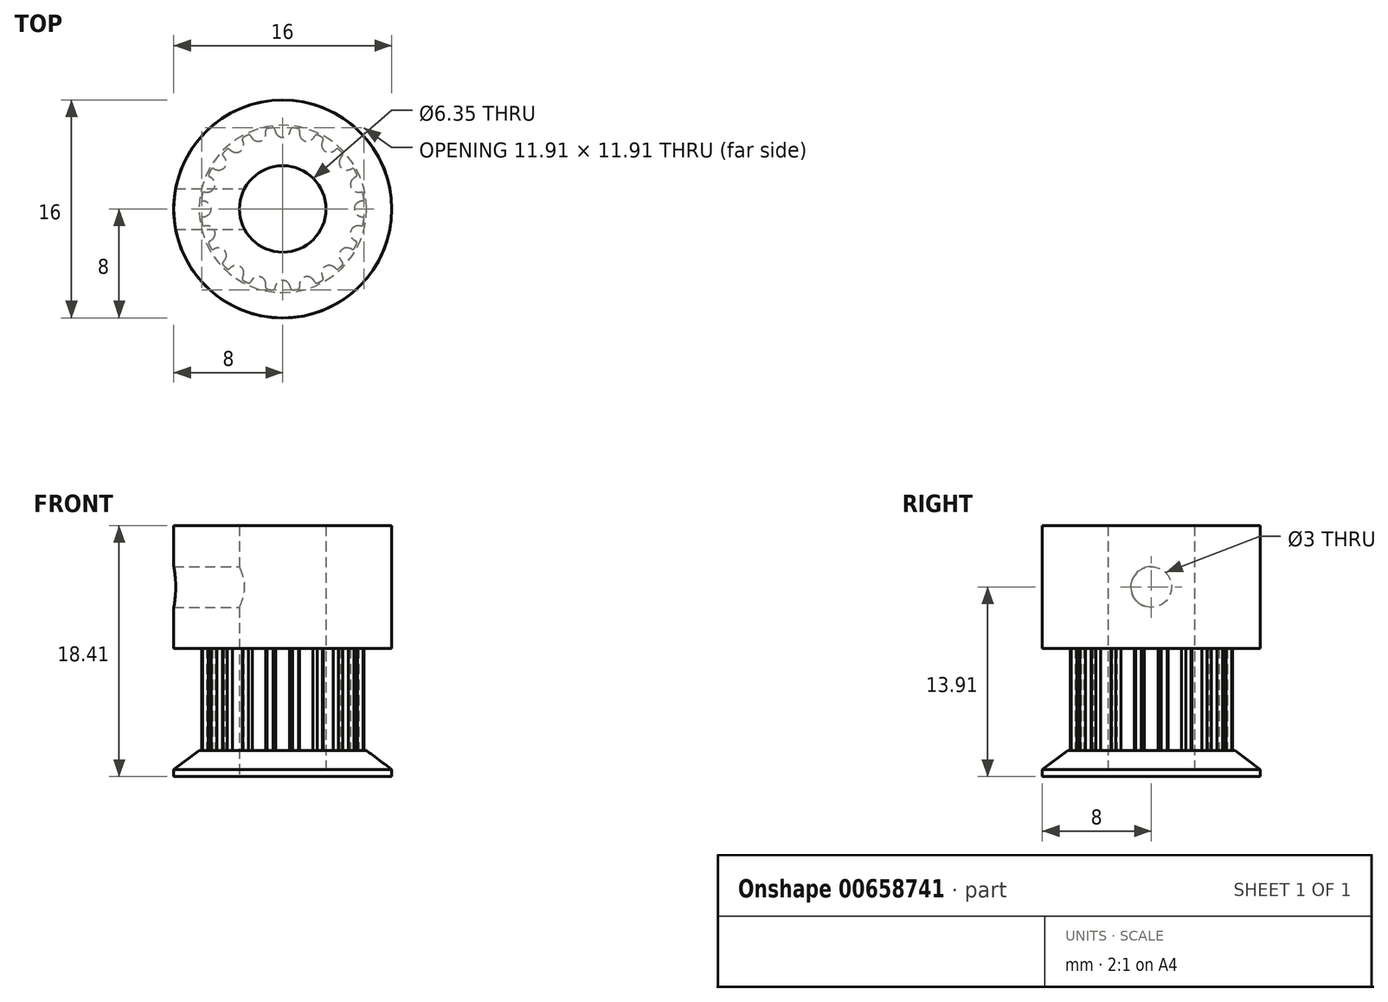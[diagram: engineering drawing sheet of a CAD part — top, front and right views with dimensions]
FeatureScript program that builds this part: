
annotation { "Feature Type Name" : "Feature", "Feature Type Description" : "" }
export const myFeature = defineFeature(function(context is Context, id is Id, definition is map)
    precondition{}
    {
        {
            var Q0;
            Q0=qCreatedBy(makeId("Top.planeOp"),FACE);
            var sketch = newSketch(context, id + "F0", { "sketchPlane" : qUnion([Q0])});
            skLineSegment(sketch, "E0", {"start": v(-19.17, 17.78) * mm, "end": v(-18.17, 17.78) * mm});
            skLineSegment(sketch, "E1", {"start": v(-18.17, 17.78) * mm, "end": v(-18.17, 18.4) * mm});
            skArc(sketch, "E2", {"start": v(-18.67, 18.85) * mm, "mid": v(-18.88, 19.07) * mm, "end": v(-19.17, 19.16) * mm});
            skArc(sketch, "E3", {"start": v(-18.58, 18.54) * mm, "mid": v(-18.61, 18.7) * mm, "end": v(-18.67, 18.85) * mm});
            skArc(sketch, "E4", {"start": v(-18.58, 18.54) * mm, "mid": v(-18.53, 18.44) * mm, "end": v(-18.43, 18.4) * mm});
            skLineSegment(sketch, "E5", {"start": v(-18.43, 18.4) * mm, "end": v(-18.17, 18.4) * mm});
            skArc(sketch, "E6.0.MirrorCS", {"start": v(-19.67, 18.85) * mm, "mid": v(-19.47, 19.07) * mm, "end": v(-19.17, 19.16) * mm});
            skArc(sketch, "E7.0.MirrorCS", {"start": v(-19.76, 18.54) * mm, "mid": v(-19.73, 18.7) * mm, "end": v(-19.67, 18.85) * mm});
            skArc(sketch, "E8.0.MirrorCS", {"start": v(-19.76, 18.54) * mm, "mid": v(-19.81, 18.44) * mm, "end": v(-19.91, 18.4) * mm});
            skLineSegment(sketch, "E9.0.MirrorCS", {"start": v(-19.91, 18.4) * mm, "end": v(-20.17, 18.4) * mm});
            skLineSegment(sketch, "E10.0.MirrorCS", {"start": v(-20.17, 17.78) * mm, "end": v(-20.17, 18.4) * mm});
            skLineSegment(sketch, "E11.0.MirrorCS", {"start": v(-19.17, 17.78) * mm, "end": v(-20.17, 17.78) * mm});
            skLineSegment(sketch, "E12.direction1", {"start": v(-20.17, 17.78) * mm, "end": v(-18.17, 17.78) * mm, "construction": true});
            skLineSegment(sketch, "E13", {"start": v(-20.17, 18.15) * mm, "end": v(-18.17, 18.15) * mm, "construction": true});
            skPoint(sketch, "E14", {"position": v(0, -5.25) * mm});
            skArc(sketch, "E15", {"start": v(0.51, -5.6) * mm, "mid": v(0, -5.25) * mm, "end": v(-0.51, -5.6) * mm});
            skArc(sketch, "E16", {"start": v(-0.51, -5.6) * mm, "mid": v(-0.56, -5.71) * mm, "end": v(-0.59, -5.83) * mm});
            skArc(sketch, "E17", {"start": v(0.59, -5.83) * mm, "mid": v(0.56, -5.71) * mm, "end": v(0.51, -5.6) * mm});
            skArc(sketch, "E18", {"start": v(0.72, -5.96) * mm, "mid": v(0.94, -5.93) * mm, "end": v(1.16, -5.89) * mm});
            skArc(sketch, "E19", {"start": v(0.59, -5.83) * mm, "mid": v(0.66, -5.94) * mm, "end": v(0.8, -5.95) * mm});
            skArc(sketch, "E20", {"start": v(-0.59, -5.83) * mm, "mid": v(-0.66, -5.94) * mm, "end": v(-0.8, -5.95) * mm});
            skArc(sketch, "E21.1.0", {"start": v(2.22, -5.16) * mm, "mid": v(1.62, -5) * mm, "end": v(1.24, -5.48) * mm});
            skPoint(sketch, "E21.1.1", {"position": v(1.62, -5) * mm});
            skArc(sketch, "E21.1.2", {"start": v(1.24, -5.48) * mm, "mid": v(1.23, -5.6) * mm, "end": v(1.24, -5.73) * mm});
            skArc(sketch, "E21.1.3", {"start": v(2.36, -5.37) * mm, "mid": v(2.47, -5.44) * mm, "end": v(2.6, -5.41) * mm});
            skArc(sketch, "E21.1.4", {"start": v(1.24, -5.73) * mm, "mid": v(1.2, -5.85) * mm, "end": v(1.08, -5.9) * mm});
            skArc(sketch, "E21.1.5", {"start": v(2.36, -5.37) * mm, "mid": v(2.3, -5.26) * mm, "end": v(2.22, -5.16) * mm});
            skArc(sketch, "E22.3.2.0", {"start": v(3.7, -4.22) * mm, "mid": v(3.09, -4.25) * mm, "end": v(2.87, -4.83) * mm});
            skPoint(sketch, "E22.4.2.0", {"position": v(3.09, -4.25) * mm});
            skArc(sketch, "E22.5.2.0", {"start": v(2.87, -4.83) * mm, "mid": v(2.9, -4.95) * mm, "end": v(2.95, -5.07) * mm});
            skArc(sketch, "E22.9.2.0", {"start": v(3.9, -4.37) * mm, "mid": v(4.03, -4.41) * mm, "end": v(4.14, -4.35) * mm});
            skArc(sketch, "E22.13.2.0", {"start": v(2.95, -5.07) * mm, "mid": v(2.95, -5.2) * mm, "end": v(2.85, -5.28) * mm});
            skArc(sketch, "E22.17.2.0", {"start": v(3.9, -4.37) * mm, "mid": v(3.81, -4.3) * mm, "end": v(3.7, -4.22) * mm});
            skArc(sketch, "E22.3.3.0", {"start": v(4.83, -2.87) * mm, "mid": v(4.25, -3.09) * mm, "end": v(4.22, -3.7) * mm});
            skPoint(sketch, "E22.4.3.0", {"position": v(4.25, -3.09) * mm});
            skArc(sketch, "E22.5.3.0", {"start": v(4.22, -3.7) * mm, "mid": v(4.3, -3.81) * mm, "end": v(4.37, -3.9) * mm});
            skArc(sketch, "E22.9.3.0", {"start": v(5.07, -2.95) * mm, "mid": v(5.2, -2.95) * mm, "end": v(5.28, -2.85) * mm});
            skArc(sketch, "E22.13.3.0", {"start": v(4.37, -3.9) * mm, "mid": v(4.41, -4.03) * mm, "end": v(4.35, -4.14) * mm});
            skArc(sketch, "E22.17.3.0", {"start": v(5.07, -2.95) * mm, "mid": v(4.95, -2.9) * mm, "end": v(4.83, -2.87) * mm});
            skArc(sketch, "E22.3.4.0", {"start": v(5.48, -1.24) * mm, "mid": v(5, -1.62) * mm, "end": v(5.16, -2.22) * mm});
            skPoint(sketch, "E22.4.4.0", {"position": v(5, -1.62) * mm});
            skArc(sketch, "E22.5.4.0", {"start": v(5.16, -2.22) * mm, "mid": v(5.26, -2.3) * mm, "end": v(5.37, -2.36) * mm});
            skArc(sketch, "E22.9.4.0", {"start": v(5.73, -1.24) * mm, "mid": v(5.85, -1.2) * mm, "end": v(5.9, -1.08) * mm});
            skArc(sketch, "E22.13.4.0", {"start": v(5.37, -2.36) * mm, "mid": v(5.44, -2.47) * mm, "end": v(5.41, -2.6) * mm});
            skArc(sketch, "E22.17.4.0", {"start": v(5.73, -1.24) * mm, "mid": v(5.6, -1.23) * mm, "end": v(5.48, -1.24) * mm});
            skArc(sketch, "E22.3.5.0", {"start": v(5.6, 0.51) * mm, "mid": v(5.25, 0) * mm, "end": v(5.6, -0.51) * mm});
            skPoint(sketch, "E22.4.5.0", {"position": v(5.25, 0) * mm});
            skArc(sketch, "E22.5.5.0", {"start": v(5.6, -0.51) * mm, "mid": v(5.71, -0.56) * mm, "end": v(5.83, -0.59) * mm});
            skArc(sketch, "E22.9.5.0", {"start": v(5.83, 0.59) * mm, "mid": v(5.94, 0.66) * mm, "end": v(5.95, 0.8) * mm});
            skArc(sketch, "E22.13.5.0", {"start": v(5.83, -0.59) * mm, "mid": v(5.94, -0.66) * mm, "end": v(5.95, -0.8) * mm});
            skArc(sketch, "E22.17.5.0", {"start": v(5.83, 0.59) * mm, "mid": v(5.71, 0.56) * mm, "end": v(5.6, 0.51) * mm});
            skArc(sketch, "E22.3.6.0", {"start": v(5.16, 2.22) * mm, "mid": v(5, 1.62) * mm, "end": v(5.48, 1.24) * mm});
            skPoint(sketch, "E22.4.6.0", {"position": v(5, 1.62) * mm});
            skArc(sketch, "E22.5.6.0", {"start": v(5.48, 1.24) * mm, "mid": v(5.6, 1.23) * mm, "end": v(5.73, 1.24) * mm});
            skArc(sketch, "E22.9.6.0", {"start": v(5.37, 2.36) * mm, "mid": v(5.44, 2.47) * mm, "end": v(5.41, 2.6) * mm});
            skArc(sketch, "E22.13.6.0", {"start": v(5.73, 1.24) * mm, "mid": v(5.85, 1.2) * mm, "end": v(5.9, 1.08) * mm});
            skArc(sketch, "E22.17.6.0", {"start": v(5.37, 2.36) * mm, "mid": v(5.26, 2.3) * mm, "end": v(5.16, 2.22) * mm});
            skArc(sketch, "E22.3.7.0", {"start": v(4.22, 3.7) * mm, "mid": v(4.25, 3.09) * mm, "end": v(4.83, 2.87) * mm});
            skPoint(sketch, "E22.4.7.0", {"position": v(4.25, 3.09) * mm});
            skArc(sketch, "E22.5.7.0", {"start": v(4.83, 2.87) * mm, "mid": v(4.95, 2.9) * mm, "end": v(5.07, 2.95) * mm});
            skArc(sketch, "E22.9.7.0", {"start": v(4.37, 3.9) * mm, "mid": v(4.41, 4.03) * mm, "end": v(4.35, 4.14) * mm});
            skArc(sketch, "E22.13.7.0", {"start": v(5.07, 2.95) * mm, "mid": v(5.2, 2.95) * mm, "end": v(5.28, 2.85) * mm});
            skArc(sketch, "E22.17.7.0", {"start": v(4.37, 3.9) * mm, "mid": v(4.3, 3.81) * mm, "end": v(4.22, 3.7) * mm});
            skArc(sketch, "E22.3.8.0", {"start": v(2.87, 4.83) * mm, "mid": v(3.09, 4.25) * mm, "end": v(3.7, 4.22) * mm});
            skPoint(sketch, "E22.4.8.0", {"position": v(3.09, 4.25) * mm});
            skArc(sketch, "E22.5.8.0", {"start": v(3.7, 4.22) * mm, "mid": v(3.81, 4.3) * mm, "end": v(3.9, 4.37) * mm});
            skArc(sketch, "E22.9.8.0", {"start": v(2.95, 5.07) * mm, "mid": v(2.95, 5.2) * mm, "end": v(2.85, 5.28) * mm});
            skArc(sketch, "E22.13.8.0", {"start": v(3.9, 4.37) * mm, "mid": v(4.03, 4.41) * mm, "end": v(4.14, 4.35) * mm});
            skArc(sketch, "E22.17.8.0", {"start": v(2.95, 5.07) * mm, "mid": v(2.9, 4.95) * mm, "end": v(2.87, 4.83) * mm});
            skArc(sketch, "E22.3.9.0", {"start": v(1.24, 5.48) * mm, "mid": v(1.62, 5) * mm, "end": v(2.22, 5.16) * mm});
            skPoint(sketch, "E22.4.9.0", {"position": v(1.62, 5) * mm});
            skArc(sketch, "E22.5.9.0", {"start": v(2.22, 5.16) * mm, "mid": v(2.3, 5.26) * mm, "end": v(2.36, 5.37) * mm});
            skArc(sketch, "E22.9.9.0", {"start": v(1.24, 5.73) * mm, "mid": v(1.2, 5.85) * mm, "end": v(1.08, 5.9) * mm});
            skArc(sketch, "E22.13.9.0", {"start": v(2.36, 5.37) * mm, "mid": v(2.47, 5.44) * mm, "end": v(2.6, 5.41) * mm});
            skArc(sketch, "E22.17.9.0", {"start": v(1.24, 5.73) * mm, "mid": v(1.23, 5.6) * mm, "end": v(1.24, 5.48) * mm});
            skArc(sketch, "E22.3.10.0", {"start": v(-0.51, 5.6) * mm, "mid": v(0, 5.25) * mm, "end": v(0.51, 5.6) * mm});
            skPoint(sketch, "E22.4.10.0", {"position": v(0, 5.25) * mm});
            skArc(sketch, "E22.5.10.0", {"start": v(0.51, 5.6) * mm, "mid": v(0.56, 5.71) * mm, "end": v(0.59, 5.83) * mm});
            skArc(sketch, "E22.9.10.0", {"start": v(-0.59, 5.83) * mm, "mid": v(-0.66, 5.94) * mm, "end": v(-0.8, 5.95) * mm});
            skArc(sketch, "E22.13.10.0", {"start": v(0.59, 5.83) * mm, "mid": v(0.66, 5.94) * mm, "end": v(0.8, 5.95) * mm});
            skArc(sketch, "E22.17.10.0", {"start": v(-0.59, 5.83) * mm, "mid": v(-0.56, 5.71) * mm, "end": v(-0.51, 5.6) * mm});
            skArc(sketch, "E22.3.11.0", {"start": v(-2.22, 5.16) * mm, "mid": v(-1.62, 5) * mm, "end": v(-1.24, 5.48) * mm});
            skPoint(sketch, "E22.4.11.0", {"position": v(-1.62, 5) * mm});
            skArc(sketch, "E22.5.11.0", {"start": v(-1.24, 5.48) * mm, "mid": v(-1.23, 5.6) * mm, "end": v(-1.24, 5.73) * mm});
            skArc(sketch, "E22.9.11.0", {"start": v(-2.36, 5.37) * mm, "mid": v(-2.47, 5.44) * mm, "end": v(-2.6, 5.41) * mm});
            skArc(sketch, "E22.13.11.0", {"start": v(-1.24, 5.73) * mm, "mid": v(-1.2, 5.85) * mm, "end": v(-1.08, 5.9) * mm});
            skArc(sketch, "E22.17.11.0", {"start": v(-2.36, 5.37) * mm, "mid": v(-2.3, 5.26) * mm, "end": v(-2.22, 5.16) * mm});
            skArc(sketch, "E22.3.12.0", {"start": v(-3.7, 4.22) * mm, "mid": v(-3.09, 4.25) * mm, "end": v(-2.87, 4.83) * mm});
            skPoint(sketch, "E22.4.12.0", {"position": v(-3.09, 4.25) * mm});
            skArc(sketch, "E22.5.12.0", {"start": v(-2.87, 4.83) * mm, "mid": v(-2.9, 4.95) * mm, "end": v(-2.95, 5.07) * mm});
            skArc(sketch, "E22.9.12.0", {"start": v(-3.9, 4.37) * mm, "mid": v(-4.03, 4.41) * mm, "end": v(-4.14, 4.35) * mm});
            skArc(sketch, "E22.13.12.0", {"start": v(-2.95, 5.07) * mm, "mid": v(-2.95, 5.2) * mm, "end": v(-2.85, 5.28) * mm});
            skArc(sketch, "E22.17.12.0", {"start": v(-3.9, 4.37) * mm, "mid": v(-3.81, 4.3) * mm, "end": v(-3.7, 4.22) * mm});
            skArc(sketch, "E22.3.13.0", {"start": v(-4.83, 2.87) * mm, "mid": v(-4.25, 3.09) * mm, "end": v(-4.22, 3.7) * mm});
            skPoint(sketch, "E22.4.13.0", {"position": v(-4.25, 3.09) * mm});
            skArc(sketch, "E22.5.13.0", {"start": v(-4.22, 3.7) * mm, "mid": v(-4.3, 3.81) * mm, "end": v(-4.37, 3.9) * mm});
            skArc(sketch, "E22.9.13.0", {"start": v(-5.07, 2.95) * mm, "mid": v(-5.2, 2.95) * mm, "end": v(-5.28, 2.85) * mm});
            skArc(sketch, "E22.13.13.0", {"start": v(-4.37, 3.9) * mm, "mid": v(-4.41, 4.03) * mm, "end": v(-4.35, 4.14) * mm});
            skArc(sketch, "E22.17.13.0", {"start": v(-5.07, 2.95) * mm, "mid": v(-4.95, 2.9) * mm, "end": v(-4.83, 2.87) * mm});
            skArc(sketch, "E22.3.14.0", {"start": v(-5.48, 1.24) * mm, "mid": v(-5, 1.62) * mm, "end": v(-5.16, 2.22) * mm});
            skPoint(sketch, "E22.4.14.0", {"position": v(-5, 1.62) * mm});
            skArc(sketch, "E22.5.14.0", {"start": v(-5.16, 2.22) * mm, "mid": v(-5.26, 2.3) * mm, "end": v(-5.37, 2.36) * mm});
            skArc(sketch, "E22.9.14.0", {"start": v(-5.73, 1.24) * mm, "mid": v(-5.85, 1.2) * mm, "end": v(-5.9, 1.08) * mm});
            skArc(sketch, "E22.13.14.0", {"start": v(-5.37, 2.36) * mm, "mid": v(-5.44, 2.47) * mm, "end": v(-5.41, 2.6) * mm});
            skArc(sketch, "E22.17.14.0", {"start": v(-5.73, 1.24) * mm, "mid": v(-5.6, 1.23) * mm, "end": v(-5.48, 1.24) * mm});
            skArc(sketch, "E22.3.15.0", {"start": v(-5.6, -0.51) * mm, "mid": v(-5.25, 0) * mm, "end": v(-5.6, 0.51) * mm});
            skPoint(sketch, "E22.4.15.0", {"position": v(-5.25, 0) * mm});
            skArc(sketch, "E22.5.15.0", {"start": v(-5.6, 0.51) * mm, "mid": v(-5.71, 0.56) * mm, "end": v(-5.83, 0.59) * mm});
            skArc(sketch, "E22.9.15.0", {"start": v(-5.83, -0.59) * mm, "mid": v(-5.94, -0.66) * mm, "end": v(-5.95, -0.8) * mm});
            skArc(sketch, "E22.13.15.0", {"start": v(-5.83, 0.59) * mm, "mid": v(-5.94, 0.66) * mm, "end": v(-5.95, 0.8) * mm});
            skArc(sketch, "E22.17.15.0", {"start": v(-5.83, -0.59) * mm, "mid": v(-5.71, -0.56) * mm, "end": v(-5.6, -0.51) * mm});
            skArc(sketch, "E22.3.16.0", {"start": v(-5.16, -2.22) * mm, "mid": v(-5, -1.62) * mm, "end": v(-5.48, -1.24) * mm});
            skPoint(sketch, "E22.4.16.0", {"position": v(-5, -1.62) * mm});
            skArc(sketch, "E22.5.16.0", {"start": v(-5.48, -1.24) * mm, "mid": v(-5.6, -1.23) * mm, "end": v(-5.73, -1.24) * mm});
            skArc(sketch, "E22.9.16.0", {"start": v(-5.37, -2.36) * mm, "mid": v(-5.44, -2.47) * mm, "end": v(-5.41, -2.6) * mm});
            skArc(sketch, "E22.13.16.0", {"start": v(-5.73, -1.24) * mm, "mid": v(-5.85, -1.2) * mm, "end": v(-5.9, -1.08) * mm});
            skArc(sketch, "E22.17.16.0", {"start": v(-5.37, -2.36) * mm, "mid": v(-5.26, -2.3) * mm, "end": v(-5.16, -2.22) * mm});
            skArc(sketch, "E22.3.17.0", {"start": v(-4.22, -3.7) * mm, "mid": v(-4.25, -3.09) * mm, "end": v(-4.83, -2.87) * mm});
            skPoint(sketch, "E22.4.17.0", {"position": v(-4.25, -3.09) * mm});
            skArc(sketch, "E22.5.17.0", {"start": v(-4.83, -2.87) * mm, "mid": v(-4.95, -2.9) * mm, "end": v(-5.07, -2.95) * mm});
            skArc(sketch, "E22.9.17.0", {"start": v(-4.37, -3.9) * mm, "mid": v(-4.41, -4.03) * mm, "end": v(-4.35, -4.14) * mm});
            skArc(sketch, "E22.13.17.0", {"start": v(-5.07, -2.95) * mm, "mid": v(-5.2, -2.95) * mm, "end": v(-5.28, -2.85) * mm});
            skArc(sketch, "E22.17.17.0", {"start": v(-4.37, -3.9) * mm, "mid": v(-4.3, -3.81) * mm, "end": v(-4.22, -3.7) * mm});
            skArc(sketch, "E22.3.18.0", {"start": v(-2.87, -4.83) * mm, "mid": v(-3.09, -4.25) * mm, "end": v(-3.7, -4.22) * mm});
            skPoint(sketch, "E22.4.18.0", {"position": v(-3.09, -4.25) * mm});
            skArc(sketch, "E22.5.18.0", {"start": v(-3.7, -4.22) * mm, "mid": v(-3.81, -4.3) * mm, "end": v(-3.9, -4.37) * mm});
            skArc(sketch, "E22.9.18.0", {"start": v(-2.95, -5.07) * mm, "mid": v(-2.95, -5.2) * mm, "end": v(-2.85, -5.28) * mm});
            skArc(sketch, "E22.13.18.0", {"start": v(-3.9, -4.37) * mm, "mid": v(-4.03, -4.41) * mm, "end": v(-4.14, -4.35) * mm});
            skArc(sketch, "E22.17.18.0", {"start": v(-2.95, -5.07) * mm, "mid": v(-2.9, -4.95) * mm, "end": v(-2.87, -4.83) * mm});
            skArc(sketch, "E22.3.19.0", {"start": v(-1.24, -5.48) * mm, "mid": v(-1.62, -5) * mm, "end": v(-2.22, -5.16) * mm});
            skPoint(sketch, "E22.4.19.0", {"position": v(-1.62, -5) * mm});
            skArc(sketch, "E22.5.19.0", {"start": v(-2.22, -5.16) * mm, "mid": v(-2.3, -5.26) * mm, "end": v(-2.36, -5.37) * mm});
            skArc(sketch, "E22.9.19.0", {"start": v(-1.24, -5.73) * mm, "mid": v(-1.2, -5.85) * mm, "end": v(-1.08, -5.9) * mm});
            skArc(sketch, "E22.13.19.0", {"start": v(-2.36, -5.37) * mm, "mid": v(-2.47, -5.44) * mm, "end": v(-2.6, -5.41) * mm});
            skArc(sketch, "E22.17.19.0", {"start": v(-1.24, -5.73) * mm, "mid": v(-1.23, -5.6) * mm, "end": v(-1.24, -5.48) * mm});
            skArc(sketch, "E23.trimOffspring", {"start": v(2.52, -5.44) * mm, "mid": v(2.72, -5.35) * mm, "end": v(2.92, -5.24) * mm});
            skArc(sketch, "E24.trimOffspring", {"start": v(4.08, -4.4) * mm, "mid": v(4.24, -4.24) * mm, "end": v(4.4, -4.08) * mm});
            skArc(sketch, "E25.trimOffspring", {"start": v(5.24, -2.92) * mm, "mid": v(5.33, -2.76) * mm, "end": v(5.41, -2.6) * mm});
            skArc(sketch, "E26.trimOffspring", {"start": v(5.89, -1.16) * mm, "mid": v(5.93, -0.94) * mm, "end": v(5.96, -0.72) * mm});
            skArc(sketch, "E27.trimOffspring", {"start": v(5.44, 2.52) * mm, "mid": v(5.35, 2.72) * mm, "end": v(5.24, 2.92) * mm});
            skArc(sketch, "E28.trimOffspring", {"start": v(4.4, 4.08) * mm, "mid": v(4.24, 4.24) * mm, "end": v(4.08, 4.4) * mm});
            skArc(sketch, "E29.trimOffspring", {"start": v(5.96, 0.72) * mm, "mid": v(5.93, 0.94) * mm, "end": v(5.89, 1.16) * mm});
            skArc(sketch, "E30.trimOffspring", {"start": v(2.92, 5.24) * mm, "mid": v(2.72, 5.35) * mm, "end": v(2.52, 5.44) * mm});
            skArc(sketch, "E31.trimOffspring", {"start": v(1.16, 5.89) * mm, "mid": v(0.94, 5.93) * mm, "end": v(0.72, 5.96) * mm});
            skArc(sketch, "E32.trimOffspring", {"start": v(-0.72, 5.96) * mm, "mid": v(-0.94, 5.93) * mm, "end": v(-1.16, 5.89) * mm});
            skArc(sketch, "E33.trimOffspring", {"start": v(-2.52, 5.44) * mm, "mid": v(-2.72, 5.35) * mm, "end": v(-2.92, 5.24) * mm});
            skArc(sketch, "E34.trimOffspring", {"start": v(-4.08, 4.4) * mm, "mid": v(-4.24, 4.24) * mm, "end": v(-4.4, 4.08) * mm});
            skArc(sketch, "E35.trimOffspring", {"start": v(-5.24, 2.92) * mm, "mid": v(-5.35, 2.72) * mm, "end": v(-5.44, 2.52) * mm});
            skArc(sketch, "E36.trimOffspring", {"start": v(-5.89, 1.16) * mm, "mid": v(-5.93, 0.94) * mm, "end": v(-5.96, 0.72) * mm});
            skArc(sketch, "E37.trimOffspring", {"start": v(-5.96, -0.72) * mm, "mid": v(-5.93, -0.94) * mm, "end": v(-5.89, -1.16) * mm});
            skArc(sketch, "E38.trimOffspring", {"start": v(-5.44, -2.52) * mm, "mid": v(-5.35, -2.72) * mm, "end": v(-5.24, -2.92) * mm});
            skArc(sketch, "E39.trimOffspring", {"start": v(-4.4, -4.08) * mm, "mid": v(-4.24, -4.24) * mm, "end": v(-4.08, -4.4) * mm});
            skArc(sketch, "E40.trimOffspring", {"start": v(-2.92, -5.24) * mm, "mid": v(-2.72, -5.35) * mm, "end": v(-2.52, -5.44) * mm});
            skArc(sketch, "E41.trimOffspring", {"start": v(-1.16, -5.89) * mm, "mid": v(-0.94, -5.93) * mm, "end": v(-0.72, -5.96) * mm});
            skSolve(sketch);
        }
        {
            var Q0;
            Q0=makeQuery(id+"F0.imprint","IMPRINT",FACE,{"disambiguationData":[TD([[makeQuery(id+"F0.imprint","IMPRINT",EDGE,{"derivedFrom":sQuery(id+"F0.wireOp",EDGE,"E15")}),-1.0]])]});
            extrude(context, id + "F1", {"entities" : qUnion([Q0]), "depth" : 7.5 * mm});
        }
        {
            var Q0;
            Q0=makeQuery(id+"F1.opExtrude","CAP_FACE",FACE,{"disambiguationData":[OSD([sQuery(id+"F0.wireOp",EDGE,"E15"),sQuery(id+"F0.wireOp",EDGE,"E16"),sQuery(id+"F0.wireOp",EDGE,"E17"),sQuery(id+"F0.wireOp",EDGE,"E18"),sQuery(id+"F0.wireOp",EDGE,"E19"),sQuery(id+"F0.wireOp",EDGE,"E20"),sQuery(id+"F0.wireOp",EDGE,"E21.1.0"),sQuery(id+"F0.wireOp",EDGE,"E21.1.2"),sQuery(id+"F0.wireOp",EDGE,"E21.1.3"),sQuery(id+"F0.wireOp",EDGE,"E21.1.4"),sQuery(id+"F0.wireOp",EDGE,"E21.1.5"),sQuery(id+"F0.wireOp",EDGE,"E22.3.2.0"),sQuery(id+"F0.wireOp",EDGE,"E22.5.2.0"),sQuery(id+"F0.wireOp",EDGE,"E22.9.2.0"),sQuery(id+"F0.wireOp",EDGE,"E22.13.2.0"),sQuery(id+"F0.wireOp",EDGE,"E22.17.2.0"),sQuery(id+"F0.wireOp",EDGE,"E22.3.3.0"),sQuery(id+"F0.wireOp",EDGE,"E22.5.3.0"),sQuery(id+"F0.wireOp",EDGE,"E22.9.3.0"),sQuery(id+"F0.wireOp",EDGE,"E22.13.3.0"),sQuery(id+"F0.wireOp",EDGE,"E22.17.3.0"),sQuery(id+"F0.wireOp",EDGE,"E22.3.4.0"),sQuery(id+"F0.wireOp",EDGE,"E22.5.4.0"),sQuery(id+"F0.wireOp",EDGE,"E22.9.4.0"),sQuery(id+"F0.wireOp",EDGE,"E22.13.4.0"),sQuery(id+"F0.wireOp",EDGE,"E22.17.4.0"),sQuery(id+"F0.wireOp",EDGE,"E22.3.5.0"),sQuery(id+"F0.wireOp",EDGE,"E22.5.5.0"),sQuery(id+"F0.wireOp",EDGE,"E22.9.5.0"),sQuery(id+"F0.wireOp",EDGE,"E22.13.5.0"),sQuery(id+"F0.wireOp",EDGE,"E22.17.5.0"),sQuery(id+"F0.wireOp",EDGE,"E22.3.6.0"),sQuery(id+"F0.wireOp",EDGE,"E22.5.6.0"),sQuery(id+"F0.wireOp",EDGE,"E22.9.6.0"),sQuery(id+"F0.wireOp",EDGE,"E22.13.6.0"),sQuery(id+"F0.wireOp",EDGE,"E22.17.6.0"),sQuery(id+"F0.wireOp",EDGE,"E22.3.7.0"),sQuery(id+"F0.wireOp",EDGE,"E22.5.7.0"),sQuery(id+"F0.wireOp",EDGE,"E22.9.7.0"),sQuery(id+"F0.wireOp",EDGE,"E22.13.7.0"),sQuery(id+"F0.wireOp",EDGE,"E22.17.7.0"),sQuery(id+"F0.wireOp",EDGE,"E22.3.8.0"),sQuery(id+"F0.wireOp",EDGE,"E22.5.8.0"),sQuery(id+"F0.wireOp",EDGE,"E22.9.8.0"),sQuery(id+"F0.wireOp",EDGE,"E22.13.8.0"),sQuery(id+"F0.wireOp",EDGE,"E22.17.8.0"),sQuery(id+"F0.wireOp",EDGE,"E22.3.9.0"),sQuery(id+"F0.wireOp",EDGE,"E22.5.9.0"),sQuery(id+"F0.wireOp",EDGE,"E22.9.9.0"),sQuery(id+"F0.wireOp",EDGE,"E22.13.9.0"),sQuery(id+"F0.wireOp",EDGE,"E22.17.9.0"),sQuery(id+"F0.wireOp",EDGE,"E22.3.10.0"),sQuery(id+"F0.wireOp",EDGE,"E22.5.10.0"),sQuery(id+"F0.wireOp",EDGE,"E22.9.10.0"),sQuery(id+"F0.wireOp",EDGE,"E22.13.10.0"),sQuery(id+"F0.wireOp",EDGE,"E22.17.10.0"),sQuery(id+"F0.wireOp",EDGE,"E22.3.11.0"),sQuery(id+"F0.wireOp",EDGE,"E22.5.11.0"),sQuery(id+"F0.wireOp",EDGE,"E22.9.11.0"),sQuery(id+"F0.wireOp",EDGE,"E22.13.11.0"),sQuery(id+"F0.wireOp",EDGE,"E22.17.11.0"),sQuery(id+"F0.wireOp",EDGE,"E22.3.12.0"),sQuery(id+"F0.wireOp",EDGE,"E22.5.12.0"),sQuery(id+"F0.wireOp",EDGE,"E22.9.12.0"),sQuery(id+"F0.wireOp",EDGE,"E22.13.12.0"),sQuery(id+"F0.wireOp",EDGE,"E22.17.12.0"),sQuery(id+"F0.wireOp",EDGE,"E22.3.13.0"),sQuery(id+"F0.wireOp",EDGE,"E22.5.13.0"),sQuery(id+"F0.wireOp",EDGE,"E22.9.13.0"),sQuery(id+"F0.wireOp",EDGE,"E22.13.13.0"),sQuery(id+"F0.wireOp",EDGE,"E22.17.13.0"),sQuery(id+"F0.wireOp",EDGE,"E22.3.14.0"),sQuery(id+"F0.wireOp",EDGE,"E22.5.14.0"),sQuery(id+"F0.wireOp",EDGE,"E22.9.14.0"),sQuery(id+"F0.wireOp",EDGE,"E22.13.14.0"),sQuery(id+"F0.wireOp",EDGE,"E22.17.14.0"),sQuery(id+"F0.wireOp",EDGE,"E22.3.15.0"),sQuery(id+"F0.wireOp",EDGE,"E22.5.15.0"),sQuery(id+"F0.wireOp",EDGE,"E22.9.15.0"),sQuery(id+"F0.wireOp",EDGE,"E22.13.15.0"),sQuery(id+"F0.wireOp",EDGE,"E22.17.15.0"),sQuery(id+"F0.wireOp",EDGE,"E22.3.16.0"),sQuery(id+"F0.wireOp",EDGE,"E22.5.16.0"),sQuery(id+"F0.wireOp",EDGE,"E22.9.16.0"),sQuery(id+"F0.wireOp",EDGE,"E22.13.16.0"),sQuery(id+"F0.wireOp",EDGE,"E22.17.16.0"),sQuery(id+"F0.wireOp",EDGE,"E22.3.17.0"),sQuery(id+"F0.wireOp",EDGE,"E22.5.17.0"),sQuery(id+"F0.wireOp",EDGE,"E22.9.17.0"),sQuery(id+"F0.wireOp",EDGE,"E22.13.17.0"),sQuery(id+"F0.wireOp",EDGE,"E22.17.17.0"),sQuery(id+"F0.wireOp",EDGE,"E22.3.18.0"),sQuery(id+"F0.wireOp",EDGE,"E22.5.18.0"),sQuery(id+"F0.wireOp",EDGE,"E22.9.18.0"),sQuery(id+"F0.wireOp",EDGE,"E22.13.18.0"),sQuery(id+"F0.wireOp",EDGE,"E22.17.18.0"),sQuery(id+"F0.wireOp",EDGE,"E22.3.19.0"),sQuery(id+"F0.wireOp",EDGE,"E22.5.19.0"),sQuery(id+"F0.wireOp",EDGE,"E22.9.19.0"),sQuery(id+"F0.wireOp",EDGE,"E22.13.19.0"),sQuery(id+"F0.wireOp",EDGE,"E22.17.19.0"),sQuery(id+"F0.wireOp",EDGE,"E23.trimOffspring"),sQuery(id+"F0.wireOp",EDGE,"E24.trimOffspring"),sQuery(id+"F0.wireOp",EDGE,"E25.trimOffspring"),sQuery(id+"F0.wireOp",EDGE,"E26.trimOffspring"),sQuery(id+"F0.wireOp",EDGE,"E27.trimOffspring"),sQuery(id+"F0.wireOp",EDGE,"E28.trimOffspring"),sQuery(id+"F0.wireOp",EDGE,"E29.trimOffspring"),sQuery(id+"F0.wireOp",EDGE,"E30.trimOffspring"),sQuery(id+"F0.wireOp",EDGE,"E31.trimOffspring"),sQuery(id+"F0.wireOp",EDGE,"E32.trimOffspring"),sQuery(id+"F0.wireOp",EDGE,"E33.trimOffspring"),sQuery(id+"F0.wireOp",EDGE,"E34.trimOffspring"),sQuery(id+"F0.wireOp",EDGE,"E35.trimOffspring"),sQuery(id+"F0.wireOp",EDGE,"E36.trimOffspring"),sQuery(id+"F0.wireOp",EDGE,"E37.trimOffspring"),sQuery(id+"F0.wireOp",EDGE,"E38.trimOffspring"),sQuery(id+"F0.wireOp",EDGE,"E39.trimOffspring"),sQuery(id+"F0.wireOp",EDGE,"E40.trimOffspring"),sQuery(id+"F0.wireOp",EDGE,"E41.trimOffspring")])],"isStart":false});
            var sketch = newSketch(context, id + "F2", { "sketchPlane" : qUnion([Q0])});
            skCircle(sketch, "E42", {"center": v(0, 0) * mm, "radius": 8 * mm});
            skSolve(sketch);
        }
        {
            var Q0;
            Q0=qSketchRegion(id+"F2",true);
            extrude(context, id + "F3", {"entities" : qUnion([Q0]), "operationType" : NewBodyOperationType.ADD, "depth" : 9 * mm});
        }
        {
            var Q0;
            Q0=makeQuery(id+"F1.opExtrude","CAP_FACE",FACE,{"disambiguationData":[OSD([sQuery(id+"F0.wireOp",EDGE,"E15"),sQuery(id+"F0.wireOp",EDGE,"E16"),sQuery(id+"F0.wireOp",EDGE,"E17"),sQuery(id+"F0.wireOp",EDGE,"E18"),sQuery(id+"F0.wireOp",EDGE,"E19"),sQuery(id+"F0.wireOp",EDGE,"E20"),sQuery(id+"F0.wireOp",EDGE,"E21.1.0"),sQuery(id+"F0.wireOp",EDGE,"E21.1.2"),sQuery(id+"F0.wireOp",EDGE,"E21.1.3"),sQuery(id+"F0.wireOp",EDGE,"E21.1.4"),sQuery(id+"F0.wireOp",EDGE,"E21.1.5"),sQuery(id+"F0.wireOp",EDGE,"E22.3.2.0"),sQuery(id+"F0.wireOp",EDGE,"E22.5.2.0"),sQuery(id+"F0.wireOp",EDGE,"E22.9.2.0"),sQuery(id+"F0.wireOp",EDGE,"E22.13.2.0"),sQuery(id+"F0.wireOp",EDGE,"E22.17.2.0"),sQuery(id+"F0.wireOp",EDGE,"E22.3.3.0"),sQuery(id+"F0.wireOp",EDGE,"E22.5.3.0"),sQuery(id+"F0.wireOp",EDGE,"E22.9.3.0"),sQuery(id+"F0.wireOp",EDGE,"E22.13.3.0"),sQuery(id+"F0.wireOp",EDGE,"E22.17.3.0"),sQuery(id+"F0.wireOp",EDGE,"E22.3.4.0"),sQuery(id+"F0.wireOp",EDGE,"E22.5.4.0"),sQuery(id+"F0.wireOp",EDGE,"E22.9.4.0"),sQuery(id+"F0.wireOp",EDGE,"E22.13.4.0"),sQuery(id+"F0.wireOp",EDGE,"E22.17.4.0"),sQuery(id+"F0.wireOp",EDGE,"E22.3.5.0"),sQuery(id+"F0.wireOp",EDGE,"E22.5.5.0"),sQuery(id+"F0.wireOp",EDGE,"E22.9.5.0"),sQuery(id+"F0.wireOp",EDGE,"E22.13.5.0"),sQuery(id+"F0.wireOp",EDGE,"E22.17.5.0"),sQuery(id+"F0.wireOp",EDGE,"E22.3.6.0"),sQuery(id+"F0.wireOp",EDGE,"E22.5.6.0"),sQuery(id+"F0.wireOp",EDGE,"E22.9.6.0"),sQuery(id+"F0.wireOp",EDGE,"E22.13.6.0"),sQuery(id+"F0.wireOp",EDGE,"E22.17.6.0"),sQuery(id+"F0.wireOp",EDGE,"E22.3.7.0"),sQuery(id+"F0.wireOp",EDGE,"E22.5.7.0"),sQuery(id+"F0.wireOp",EDGE,"E22.9.7.0"),sQuery(id+"F0.wireOp",EDGE,"E22.13.7.0"),sQuery(id+"F0.wireOp",EDGE,"E22.17.7.0"),sQuery(id+"F0.wireOp",EDGE,"E22.3.8.0"),sQuery(id+"F0.wireOp",EDGE,"E22.5.8.0"),sQuery(id+"F0.wireOp",EDGE,"E22.9.8.0"),sQuery(id+"F0.wireOp",EDGE,"E22.13.8.0"),sQuery(id+"F0.wireOp",EDGE,"E22.17.8.0"),sQuery(id+"F0.wireOp",EDGE,"E22.3.9.0"),sQuery(id+"F0.wireOp",EDGE,"E22.5.9.0"),sQuery(id+"F0.wireOp",EDGE,"E22.9.9.0"),sQuery(id+"F0.wireOp",EDGE,"E22.13.9.0"),sQuery(id+"F0.wireOp",EDGE,"E22.17.9.0"),sQuery(id+"F0.wireOp",EDGE,"E22.3.10.0"),sQuery(id+"F0.wireOp",EDGE,"E22.5.10.0"),sQuery(id+"F0.wireOp",EDGE,"E22.9.10.0"),sQuery(id+"F0.wireOp",EDGE,"E22.13.10.0"),sQuery(id+"F0.wireOp",EDGE,"E22.17.10.0"),sQuery(id+"F0.wireOp",EDGE,"E22.3.11.0"),sQuery(id+"F0.wireOp",EDGE,"E22.5.11.0"),sQuery(id+"F0.wireOp",EDGE,"E22.9.11.0"),sQuery(id+"F0.wireOp",EDGE,"E22.13.11.0"),sQuery(id+"F0.wireOp",EDGE,"E22.17.11.0"),sQuery(id+"F0.wireOp",EDGE,"E22.3.12.0"),sQuery(id+"F0.wireOp",EDGE,"E22.5.12.0"),sQuery(id+"F0.wireOp",EDGE,"E22.9.12.0"),sQuery(id+"F0.wireOp",EDGE,"E22.13.12.0"),sQuery(id+"F0.wireOp",EDGE,"E22.17.12.0"),sQuery(id+"F0.wireOp",EDGE,"E22.3.13.0"),sQuery(id+"F0.wireOp",EDGE,"E22.5.13.0"),sQuery(id+"F0.wireOp",EDGE,"E22.9.13.0"),sQuery(id+"F0.wireOp",EDGE,"E22.13.13.0"),sQuery(id+"F0.wireOp",EDGE,"E22.17.13.0"),sQuery(id+"F0.wireOp",EDGE,"E22.3.14.0"),sQuery(id+"F0.wireOp",EDGE,"E22.5.14.0"),sQuery(id+"F0.wireOp",EDGE,"E22.9.14.0"),sQuery(id+"F0.wireOp",EDGE,"E22.13.14.0"),sQuery(id+"F0.wireOp",EDGE,"E22.17.14.0"),sQuery(id+"F0.wireOp",EDGE,"E22.3.15.0"),sQuery(id+"F0.wireOp",EDGE,"E22.5.15.0"),sQuery(id+"F0.wireOp",EDGE,"E22.9.15.0"),sQuery(id+"F0.wireOp",EDGE,"E22.13.15.0"),sQuery(id+"F0.wireOp",EDGE,"E22.17.15.0"),sQuery(id+"F0.wireOp",EDGE,"E22.3.16.0"),sQuery(id+"F0.wireOp",EDGE,"E22.5.16.0"),sQuery(id+"F0.wireOp",EDGE,"E22.9.16.0"),sQuery(id+"F0.wireOp",EDGE,"E22.13.16.0"),sQuery(id+"F0.wireOp",EDGE,"E22.17.16.0"),sQuery(id+"F0.wireOp",EDGE,"E22.3.17.0"),sQuery(id+"F0.wireOp",EDGE,"E22.5.17.0"),sQuery(id+"F0.wireOp",EDGE,"E22.9.17.0"),sQuery(id+"F0.wireOp",EDGE,"E22.13.17.0"),sQuery(id+"F0.wireOp",EDGE,"E22.17.17.0"),sQuery(id+"F0.wireOp",EDGE,"E22.3.18.0"),sQuery(id+"F0.wireOp",EDGE,"E22.5.18.0"),sQuery(id+"F0.wireOp",EDGE,"E22.9.18.0"),sQuery(id+"F0.wireOp",EDGE,"E22.13.18.0"),sQuery(id+"F0.wireOp",EDGE,"E22.17.18.0"),sQuery(id+"F0.wireOp",EDGE,"E22.3.19.0"),sQuery(id+"F0.wireOp",EDGE,"E22.5.19.0"),sQuery(id+"F0.wireOp",EDGE,"E22.9.19.0"),sQuery(id+"F0.wireOp",EDGE,"E22.13.19.0"),sQuery(id+"F0.wireOp",EDGE,"E22.17.19.0"),sQuery(id+"F0.wireOp",EDGE,"E23.trimOffspring"),sQuery(id+"F0.wireOp",EDGE,"E24.trimOffspring"),sQuery(id+"F0.wireOp",EDGE,"E25.trimOffspring"),sQuery(id+"F0.wireOp",EDGE,"E26.trimOffspring"),sQuery(id+"F0.wireOp",EDGE,"E27.trimOffspring"),sQuery(id+"F0.wireOp",EDGE,"E28.trimOffspring"),sQuery(id+"F0.wireOp",EDGE,"E29.trimOffspring"),sQuery(id+"F0.wireOp",EDGE,"E30.trimOffspring"),sQuery(id+"F0.wireOp",EDGE,"E31.trimOffspring"),sQuery(id+"F0.wireOp",EDGE,"E32.trimOffspring"),sQuery(id+"F0.wireOp",EDGE,"E33.trimOffspring"),sQuery(id+"F0.wireOp",EDGE,"E34.trimOffspring"),sQuery(id+"F0.wireOp",EDGE,"E35.trimOffspring"),sQuery(id+"F0.wireOp",EDGE,"E36.trimOffspring"),sQuery(id+"F0.wireOp",EDGE,"E37.trimOffspring"),sQuery(id+"F0.wireOp",EDGE,"E38.trimOffspring"),sQuery(id+"F0.wireOp",EDGE,"E39.trimOffspring"),sQuery(id+"F0.wireOp",EDGE,"E40.trimOffspring"),sQuery(id+"F0.wireOp",EDGE,"E41.trimOffspring")])],"isStart":true});
            var sketch = newSketch(context, id + "F4", { "sketchPlane" : qUnion([Q0])});
            skCircle(sketch, "E43", {"center": v(0, 0) * mm, "radius": 8 * mm});
            skSolve(sketch);
        }
        {
            var Q0;
            Q0=qSketchRegion(id+"F4",true);
            extrude(context, id + "F5", {"entities" : qUnion([Q0]), "operationType" : NewBodyOperationType.ADD, "depth" : 1.5 * mm});
        }
        {
            var Q0;
            Q0=makeQuery(id+"F5.opExtrude","CAP_FACE",FACE,{"disambiguationData":[OSD([sQuery(id+"F4.wireOp",EDGE,"E43")])],"isStart":false});
            var sketch = newSketch(context, id + "F6", { "sketchPlane" : qUnion([Q0])});
            skCircle(sketch, "E44", {"center": v(0, 0) * mm, "radius": 2.5 * mm});
            skSolve(sketch);
        }
        {
            var Q0;
            Q0=qSketchRegion(id+"F6",true);
            extrude(context, id + "F7", {"entities" : qUnion([Q0]), "operationType" : NewBodyOperationType.REMOVE, "endBound" : BoundingType.THROUGH_ALL, "oppositeDirection" : true, "depth" : 25 * mm});
        }
        {
            var Q0;
            Q0=qCreatedBy(makeId("Right.planeOp"),FACE);
            var sketch = newSketch(context, id + "F8", { "sketchPlane" : qUnion([Q0])});
            skCircle(sketch, "E45", {"center": v(0, 12) * mm, "radius": 1.5 * mm});
            skSolve(sketch);
        }
        {
            var Q0;
            Q0=qSketchRegion(id+"F8",true);
            extrude(context, id + "F9", {"entities" : qUnion([Q0]), "operationType" : NewBodyOperationType.REMOVE, "endBound" : BoundingType.THROUGH_ALL, "oppositeDirection" : true, "depth" : 25 * mm});
        }
        {
            var Q0;
            Q0=qCreatedBy(makeId("Top.planeOp"),FACE);
            var sketch = newSketch(context, id + "F10", { "sketchPlane" : qUnion([Q0])});
            skCircle(sketch, "E46", {"center": v(0, 0) * mm, "radius": 3.18 * mm});
            skSolve(sketch);
        }
        {
            var Q0;
            Q0=qSketchRegion(id+"F10",true);
            extrude(context, id + "F11", {"entities" : qUnion([Q0]), "operationType" : NewBodyOperationType.REMOVE, "endBound" : BoundingType.SYMMETRIC, "depth" : 50.8 * mm, "offsetDistance" : 25 * mm});
        }
        {
            var Q0;
            Q0=makeQuery(id+"F5.opExtrude","CAP_FACE",FACE,{"disambiguationData":[OSD([sQuery(id+"F4.wireOp",EDGE,"E43")])],"isStart":false});
            var sketch = newSketch(context, id + "F12", { "sketchPlane" : qUnion([Q0])});
            skCircle(sketch, "E47.0.0", {"center": v(0, 0) * mm, "radius": 8 * mm});
            skSolve(sketch);
        }
        {
            var Q0;
            Q0=qSketchRegion(id+"F12",true);
            var Q1;
            Q1=makeQuery(id+"F5.opExtrude","CAP_FACE",FACE,{"disambiguationData":[OSD([sQuery(id+"F4.wireOp",EDGE,"E43")])],"isStart":true});
            extrude(context, id + "F13", {"entities" : qUnion([Q0]), "operationType" : NewBodyOperationType.REMOVE, "endBound" : BoundingType.UP_TO_SURFACE, "oppositeDirection" : true, "depth" : 25.4 * mm, "endBoundEntityFace" : qUnion([Q1]), "offsetDistance" : 25.4 * mm});
        }
        {
            var Q0;
            Q0=qCreatedBy(makeId("Front.planeOp"),FACE);
            var sketch = newSketch(context, id + "F14", { "sketchPlane" : qUnion([Q0])});
            skLineSegment(sketch, "E48", {"start": v(3.18, 0) * mm, "end": v(6.14, 0) * mm});
            skLineSegment(sketch, "E49", {"start": v(6.14, 0) * mm, "end": v(8, -1.4) * mm});
            skLineSegment(sketch, "E50", {"start": v(8, -1.4) * mm, "end": v(8, -1.9) * mm});
            skLineSegment(sketch, "E51", {"start": v(8, -1.9) * mm, "end": v(3.17, -1.9) * mm});
            skLineSegment(sketch, "E52", {"start": v(3.18, -1.9) * mm, "end": v(3.18, 0) * mm});
            skLineSegment(sketch, "E53", {"start": v(0, 0) * mm, "end": v(0, -2.56) * mm, "construction": true});
            skSolve(sketch);
        }
        {
            var Q0;
            Q0=qSketchRegion(id+"F14",true);
            var Q1;
            Q1=sQuery(id+"F14.wireOp",EDGE,"E53");
            revolve(context, id + "F15", {"operationType" : NewBodyOperationType.ADD, "entities" : qUnion([Q0]), "axis" : qUnion([Q1]), "revolveType" : RevolveType.FULL});
        }
    });
